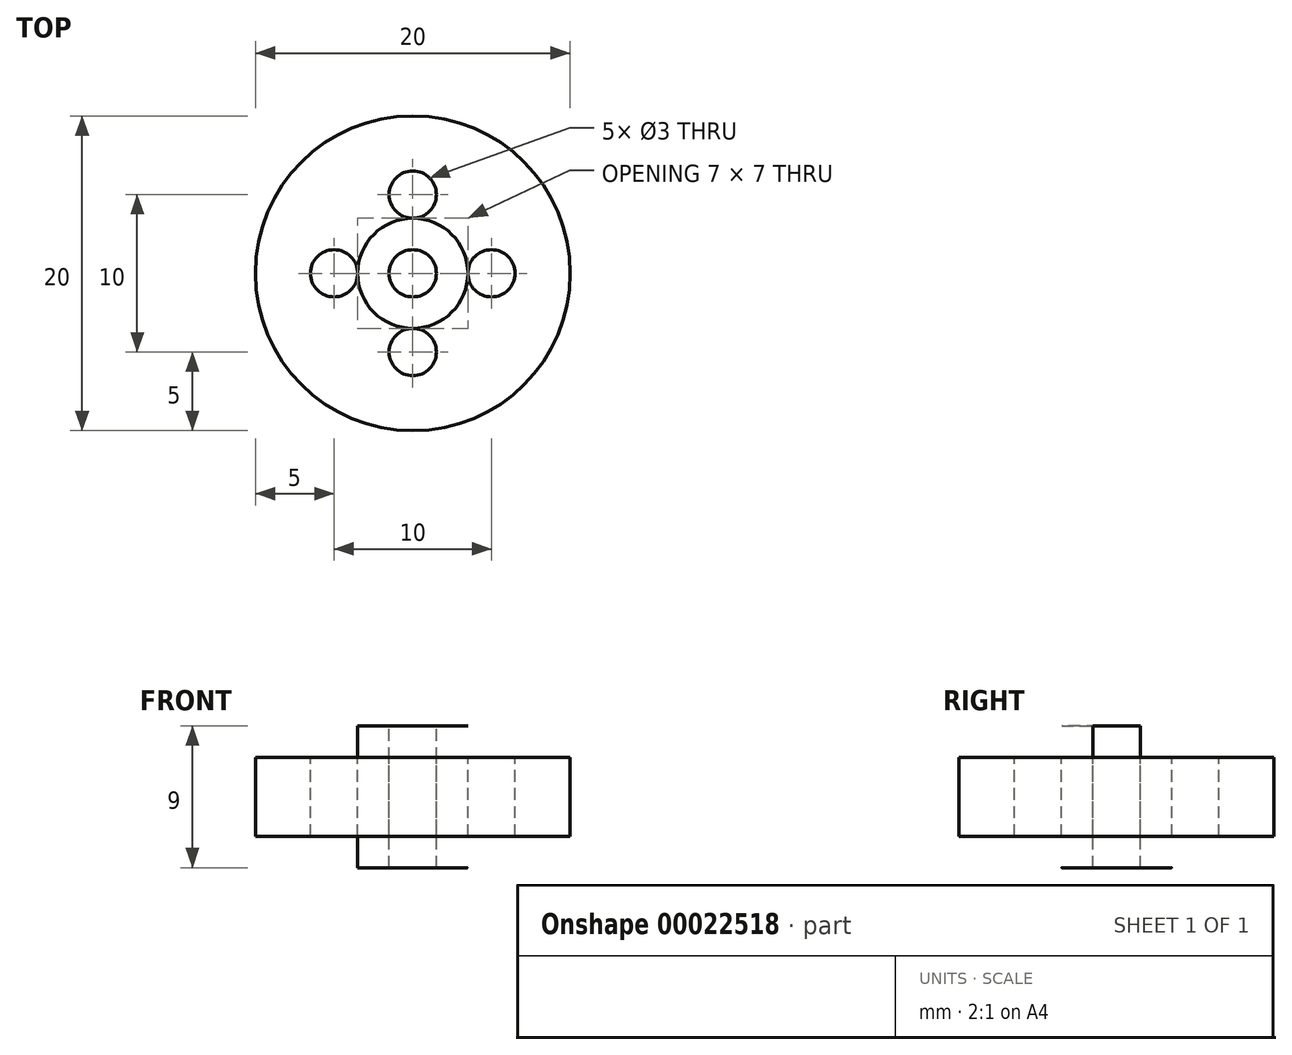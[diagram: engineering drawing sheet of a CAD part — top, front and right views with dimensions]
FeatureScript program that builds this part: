
annotation { "Feature Type Name" : "Feature", "Feature Type Description" : "" }
export const myFeature = defineFeature(function(context is Context, id is Id, definition is map)
    precondition{}
    {
        {
            var Q0;
            Q0=qCreatedBy(makeId("Top.planeOp"),FACE);
            var sketch = newSketch(context, id + "F0", { "sketchPlane" : qUnion([Q0])});
            skCircle(sketch, "E0", {"center": v(0, 0) * mm, "radius": 10 * mm});
            skSolve(sketch);
        }
        {
            var Q0;
            Q0=qSketchRegion(id+"F0",true);
            extrude(context, id + "F1", {"entities" : qUnion([Q0]), "depth" : 5 * mm});
        }
        {
            var Q0;
            Q0=makeQuery(id+"F1.opExtrude","CAP_FACE",FACE,{"disambiguationData":[OSD([sQuery(id+"F0.wireOp",EDGE,"E0")])],"isStart":false});
            var sketch = newSketch(context, id + "F2", { "sketchPlane" : qUnion([Q0])});
            skLineSegment(sketch, "E1", {"start": v(0, 10) * mm, "end": v(0, 5) * mm});
            skCircle(sketch, "E2", {"center": v(0, 5) * mm, "radius": 1.5 * mm});
            skCircle(sketch, "E3.1.0", {"center": v(-5, 0) * mm, "radius": 1.5 * mm});
            skCircle(sketch, "E3.2.0", {"center": v(0, -5) * mm, "radius": 1.5 * mm});
            skCircle(sketch, "E3.3.0", {"center": v(5, 0) * mm, "radius": 1.5 * mm});
            skPoint(sketch, "E3.center", {"position": v(0, 0) * mm});
            skCircle(sketch, "E4", {"center": v(0, 0) * mm, "radius": 3.5 * mm});
            skSolve(sketch);
        }
        {
            var Q0;
            Q0=makeQuery(id+"F2.imprint","IMPRINT",FACE,{"disambiguationData":[TD([[makeQuery(id+"F2.imprint","IMPRINT",EDGE,{"derivedFrom":sQuery(id+"F2.wireOp",EDGE,"E4")}),1.0]])]});
            extrude(context, id + "F3", {"entities" : qUnion([Q0]), "operationType" : NewBodyOperationType.ADD, "depth" : 2 * mm});
        }
        {
            var Q0;
            Q0=makeQuery(id+"F2.imprint","IMPRINT",FACE,{"disambiguationData":[TD([[makeQuery(id+"F2.imprint","IMPRINT",EDGE,{"derivedFrom":sQuery(id+"F2.wireOp",EDGE,"E2")}),1.0]])]});
            var Q1;
            Q1=makeQuery(id+"F2.imprint","IMPRINT",FACE,{"disambiguationData":[TD([[makeQuery(id+"F2.imprint","IMPRINT",EDGE,{"derivedFrom":sQuery(id+"F2.wireOp",EDGE,"E3.1.0")}),1.0]])]});
            var Q2;
            Q2=makeQuery(id+"F2.imprint","IMPRINT",FACE,{"disambiguationData":[TD([[makeQuery(id+"F2.imprint","IMPRINT",EDGE,{"derivedFrom":sQuery(id+"F2.wireOp",EDGE,"E3.2.0")}),1.0]])]});
            var Q3;
            Q3=makeQuery(id+"F2.imprint","IMPRINT",FACE,{"disambiguationData":[TD([[makeQuery(id+"F2.imprint","IMPRINT",EDGE,{"derivedFrom":sQuery(id+"F2.wireOp",EDGE,"E3.3.0")}),1.0]])]});
            extrude(context, id + "F4", {"entities" : qUnion([Q0, Q1, Q2, Q3]), "operationType" : NewBodyOperationType.REMOVE, "oppositeDirection" : true, "depth" : 5 * mm});
        }
        {
            var Q0;
            Q0=makeQuery(id+"F3.opExtrude","CAP_FACE",FACE,{"disambiguationData":[OSD([sQuery(id+"F2.wireOp",EDGE,"E4")])],"isStart":false});
            var sketch = newSketch(context, id + "F5", { "sketchPlane" : qUnion([Q0])});
            skCircle(sketch, "E5", {"center": v(0, 0) * mm, "radius": 1.5 * mm});
            skSolve(sketch);
        }
        {
            var Q0;
            Q0=makeQuery(id+"F5.imprint","IMPRINT",FACE,{"disambiguationData":[TD([[makeQuery(id+"F5.imprint","IMPRINT",EDGE,{"derivedFrom":sQuery(id+"F5.wireOp",EDGE,"E5")}),1.0]])]});
            extrude(context, id + "F6", {"entities" : qUnion([Q0]), "operationType" : NewBodyOperationType.REMOVE, "oppositeDirection" : true, "depth" : 10 * mm});
        }
        {
            var Q0;
            Q0=makeQuery(id+"F1.opExtrude","SWEPT_BODY",BODY,{"disambiguationData":[OSD([sQuery(id+"F0.wireOp",EDGE,"E0")])]});
            transform(context, id + "F7", {"entities" : qUnion([Q0]), "transformType" : TransformType.TRANSLATION_3D, "dx" : 0 * mm, "dy" : 0 * mm, "dz" : 0 * mm, "makeCopy" : true});
        }
        {
            var Q0;
            Q0=makeQuery(id+"F7.opPattern","COPY",BODY,{"derivedFrom":makeQuery(id+"F1.opExtrude","SWEPT_BODY",BODY,{"disambiguationData":[OSD([sQuery(id+"F0.wireOp",EDGE,"E0")])]}),"instanceName":"1"});
            transform(context, id + "F8", {"entities" : qUnion([Q0]), "transformType" : TransformType.TRANSLATION_3D, "dx" : 0 * mm, "dy" : 0 * mm, "dz" : 0 * mm, "makeCopy" : true});
        }
        {
            var Q0;
            Q0=makeQuery(id+"F1.opExtrude","CAP_FACE",FACE,{"disambiguationData":[OSD([sQuery(id+"F0.wireOp",EDGE,"E0")])],"isStart":true});
            var sketch = newSketch(context, id + "F9", { "sketchPlane" : qUnion([Q0])});
            skCircle(sketch, "E6", {"center": v(0, 0) * mm, "radius": 3.5 * mm});
            skSolve(sketch);
        }
        {
            var Q0;
            Q0=makeQuery(id+"F9.imprint","IMPRINT",FACE,{"disambiguationData":[TD([[makeQuery(id+"F9.imprint","IMPRINT",EDGE,{"derivedFrom":makeQuery(id+"F6.boolean.opBoolean","INTERSECT",EDGE,{"derivedFrom":[makeQuery(id+"F1.opExtrude","CAP_FACE",FACE,{"disambiguationData":[OSD([sQuery(id+"F0.wireOp",EDGE,"E0")])],"isStart":true}),makeQuery(id+"F6.opExtrude","SWEPT_FACE",FACE,{"disambiguationData":[OSD([sQuery(id+"F5.wireOp",EDGE,"E5")])]})]})}),1.0]])]});
            extrude(context, id + "F10", {"entities" : qUnion([Q0]), "operationType" : NewBodyOperationType.ADD, "depth" : 2 * mm});
        }
    });
